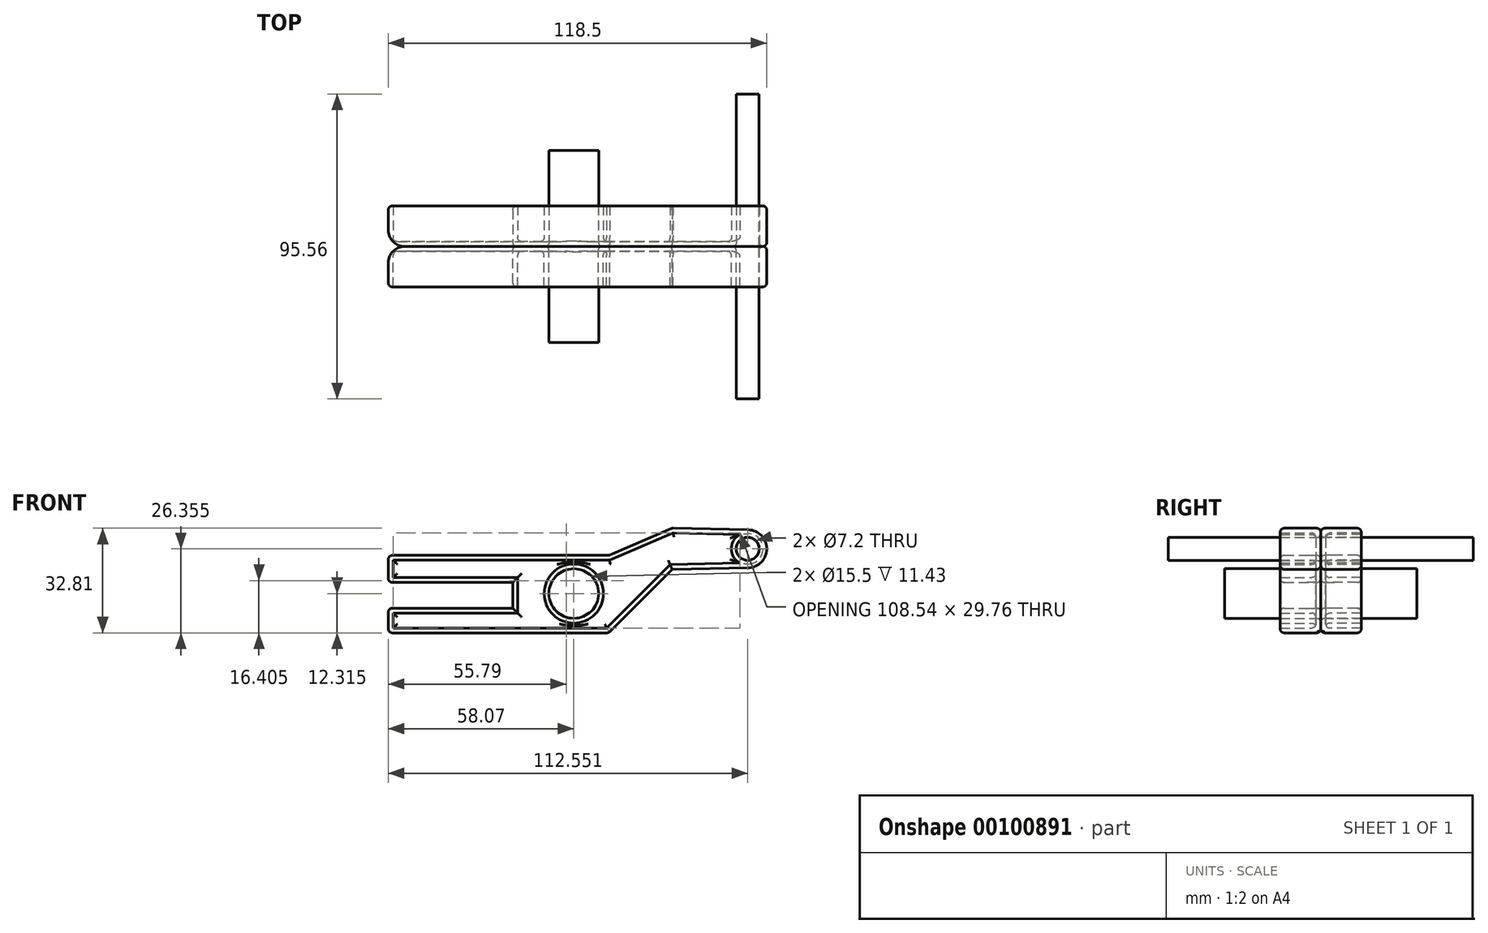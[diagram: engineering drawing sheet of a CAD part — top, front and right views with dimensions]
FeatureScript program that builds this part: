
annotation { "Feature Type Name" : "Feature", "Feature Type Description" : "" }
export const myFeature = defineFeature(function(context is Context, id is Id, definition is map)
    precondition{}
    {
        {
            var Q0;
            Q0=qCreatedBy(makeId("Front.planeOp"),FACE);
            var sketch = newSketch(context, id + "F0", { "sketchPlane" : qUnion([Q0])});
            skLineSegment(sketch, "E0", {"start": v(-58.07, -43.98) * mm, "end": v(10.9, -43.98) * mm});
            skLineSegment(sketch, "E1", {"start": v(10.9, -43.98) * mm, "end": v(30.82, -24.09) * mm});
            skLineSegment(sketch, "E2", {"start": v(30.82, -24.09) * mm, "end": v(54.61, -23.57) * mm});
            skArc(sketch, "E3", {"start": v(54.61, -23.57) * mm, "mid": v(60.43, -17.63) * mm, "end": v(54.61, -11.68) * mm});
            skLineSegment(sketch, "E4", {"start": v(54.61, -11.68) * mm, "end": v(30.82, -11.16) * mm});
            skLineSegment(sketch, "E5", {"start": v(30.82, -11.16) * mm, "end": v(10.9, -19.7) * mm});
            skLineSegment(sketch, "E6", {"start": v(10.9, -19.7) * mm, "end": v(-58.07, -19.7) * mm});
            skLineSegment(sketch, "E7", {"start": v(-58.07, -19.7) * mm, "end": v(-58.07, -28.18) * mm});
            skLineSegment(sketch, "E8", {"start": v(-58.07, -28.18) * mm, "end": v(-19.1, -28.18) * mm});
            skLineSegment(sketch, "E9", {"start": v(-19.1, -28.18) * mm, "end": v(-19.1, -36.23) * mm});
            skLineSegment(sketch, "E10", {"start": v(-19.1, -36.23) * mm, "end": v(-58.07, -36.23) * mm});
            skLineSegment(sketch, "E11", {"start": v(-58.07, -36.23) * mm, "end": v(-58.07, -43.98) * mm});
            skCircle(sketch, "E12", {"center": v(54.48, -17.63) * mm, "radius": 3.6 * mm});
            skCircle(sketch, "E13", {"center": v(0, -31.67) * mm, "radius": 7.75 * mm});
            skSolve(sketch);
        }
        {
            var Q0;
            Q0=makeQuery(id+"F0.imprint","IMPRINT",FACE,{"disambiguationData":[TD([[makeQuery(id+"F0.imprint","IMPRINT",EDGE,{"derivedFrom":sQuery(id+"F0.wireOp",EDGE,"E0")}),1.0]])]});
            extrude(context, id + "F1", {"entities" : qUnion([Q0]), "depth" : 12.7 * mm});
        }
        {
            var Q0;
            Q0=makeQuery(id+"F1.opExtrude","CAP_FACE",FACE,{"disambiguationData":[OSD([sQuery(id+"F0.wireOp",EDGE,"E0"),sQuery(id+"F0.wireOp",EDGE,"E1"),sQuery(id+"F0.wireOp",EDGE,"E2"),sQuery(id+"F0.wireOp",EDGE,"E3"),sQuery(id+"F0.wireOp",EDGE,"E4"),sQuery(id+"F0.wireOp",EDGE,"E5"),sQuery(id+"F0.wireOp",EDGE,"E6"),sQuery(id+"F0.wireOp",EDGE,"E7"),sQuery(id+"F0.wireOp",EDGE,"E8"),sQuery(id+"F0.wireOp",EDGE,"E9"),sQuery(id+"F0.wireOp",EDGE,"E10"),sQuery(id+"F0.wireOp",EDGE,"E11"),sQuery(id+"F0.wireOp",EDGE,"E12"),sQuery(id+"F0.wireOp",EDGE,"E13")])],"isStart":false});
            shell(context, id + "F2", {"entities" : qUnion([Q0]), "thickness" : 1.52 * mm});
        }
        {
            var Q0;
            {var subQ0=sQuery(id+"F0.wireOp",EDGE,"E13");var subQ1=sQuery(id+"F0.wireOp",EDGE,"E12");var subQ2=sQuery(id+"F0.wireOp",EDGE,"E11");var subQ3=sQuery(id+"F0.wireOp",EDGE,"E10");var subQ4=sQuery(id+"F0.wireOp",EDGE,"E9");var subQ5=sQuery(id+"F0.wireOp",EDGE,"E8");var subQ6=sQuery(id+"F0.wireOp",EDGE,"E7");var subQ7=sQuery(id+"F0.wireOp",EDGE,"E6");var subQ8=sQuery(id+"F0.wireOp",EDGE,"E5");var subQ9=sQuery(id+"F0.wireOp",EDGE,"E4");var subQ10=sQuery(id+"F0.wireOp",EDGE,"E3");var subQ11=sQuery(id+"F0.wireOp",EDGE,"E2");var subQ12=sQuery(id+"F0.wireOp",EDGE,"E1");var subQ13=sQuery(id+"F0.wireOp",EDGE,"E0");Q0=makeQuery(id+"F2.opShell","OFFSET_FACE",FACE,{"disambiguationData":[OSD([subQ13,subQ12,subQ11,subQ10,subQ9,subQ8,subQ7,subQ6,subQ5,subQ4,subQ3,subQ2,subQ1,subQ0]),TDD([makeQuery(id+"F1.opExtrude","CAP_FACE",FACE,{"disambiguationData":[OSD([subQ13,subQ12,subQ11,subQ10,subQ9,subQ8,subQ7,subQ6,subQ5,subQ4,subQ3,subQ2,subQ1,subQ0])],"isStart":true})])]});}
            fillet(context, id + "F10", {"entities" : qUnion([Q0]), "radius" : 1.27 * mm, "tangentPropagation" : true, "allowEdgeOverflow" : false});
        }
        {
            var Q0;
            Q0=makeQuery(id+"F1.opExtrude","CAP_EDGE",EDGE,{"disambiguationData":[OSD([sQuery(id+"F0.wireOp",EDGE,"E11")])],"isStart":true});
            var Q1;
            Q1=makeQuery(id+"F1.opExtrude","CAP_EDGE",EDGE,{"disambiguationData":[OSD([sQuery(id+"F0.wireOp",EDGE,"E7")])],"isStart":true});
            fillet(context, id + "F3", {"entities" : qUnion([Q0, Q1]), "radius" : 5.08 * mm, "tangentPropagation" : true, "allowEdgeOverflow" : false});
        }
        {
            var Q0;
            Q0=makeQuery(id+"F1.opExtrude","CAP_EDGE",EDGE,{"disambiguationData":[OSD([sQuery(id+"F0.wireOp",EDGE,"E3")])],"isStart":true});
            var Q1;
            Q1=makeQuery(id+"F1.opExtrude","SWEPT_FACE",FACE,{"disambiguationData":[OSD([sQuery(id+"F0.wireOp",EDGE,"E5")])]});
            var Q2;
            Q2=makeQuery(id+"F1.opExtrude","SWEPT_FACE",FACE,{"disambiguationData":[OSD([sQuery(id+"F0.wireOp",EDGE,"E4")])]});
            var Q3;
            Q3=makeQuery(id+"F1.opExtrude","CAP_FACE",FACE,{"disambiguationData":[OSD([sQuery(id+"F0.wireOp",EDGE,"E0"),sQuery(id+"F0.wireOp",EDGE,"E1"),sQuery(id+"F0.wireOp",EDGE,"E2"),sQuery(id+"F0.wireOp",EDGE,"E3"),sQuery(id+"F0.wireOp",EDGE,"E4"),sQuery(id+"F0.wireOp",EDGE,"E5"),sQuery(id+"F0.wireOp",EDGE,"E6"),sQuery(id+"F0.wireOp",EDGE,"E7"),sQuery(id+"F0.wireOp",EDGE,"E8"),sQuery(id+"F0.wireOp",EDGE,"E9"),sQuery(id+"F0.wireOp",EDGE,"E10"),sQuery(id+"F0.wireOp",EDGE,"E11"),sQuery(id+"F0.wireOp",EDGE,"E12"),sQuery(id+"F0.wireOp",EDGE,"E13")])],"isStart":true});
            fillet(context, id + "F11", {"entities" : qUnion([Q0, Q1, Q2, Q3]), "radius" : 1.27 * mm, "tangentPropagation" : true, "allowEdgeOverflow" : false});
        }
        {
            var Q0;
            Q0=makeQuery(id+"F1.opExtrude","CAP_EDGE",EDGE,{"disambiguationData":[OSD([sQuery(id+"F0.wireOp",EDGE,"E1")])],"isStart":false});
            var Q1;
            Q1=makeQuery(id+"F1.opExtrude","SWEPT_FACE",FACE,{"disambiguationData":[OSD([sQuery(id+"F0.wireOp",EDGE,"E0")])]});
            fillet(context, id + "F4", {"entities" : qUnion([Q0, Q1]), "radius" : 1.27 * mm, "tangentPropagation" : true, "allowEdgeOverflow" : false});
        }
        {
            var Q0;
            Q0=makeQuery(id+"F1.opExtrude","CAP_EDGE",EDGE,{"disambiguationData":[OSD([sQuery(id+"F0.wireOp",EDGE,"E9")])],"isStart":false});
            var Q1;
            Q1=makeQuery(id+"F1.opExtrude","CAP_EDGE",EDGE,{"disambiguationData":[OSD([sQuery(id+"F0.wireOp",EDGE,"E8")])],"isStart":false});
            fillet(context, id + "F5", {"entities" : qUnion([Q0, Q1]), "radius" : 1.27 * mm, "tangentPropagation" : true, "allowEdgeOverflow" : false});
        }
        {
            var Q0;
            Q0=makeQuery(id+"F1.opExtrude","SWEPT_BODY",BODY,{"disambiguationData":[OSD([sQuery(id+"F0.wireOp",EDGE,"E0"),sQuery(id+"F0.wireOp",EDGE,"E1"),sQuery(id+"F0.wireOp",EDGE,"E2"),sQuery(id+"F0.wireOp",EDGE,"E3"),sQuery(id+"F0.wireOp",EDGE,"E4"),sQuery(id+"F0.wireOp",EDGE,"E5"),sQuery(id+"F0.wireOp",EDGE,"E6"),sQuery(id+"F0.wireOp",EDGE,"E7"),sQuery(id+"F0.wireOp",EDGE,"E8"),sQuery(id+"F0.wireOp",EDGE,"E9"),sQuery(id+"F0.wireOp",EDGE,"E10"),sQuery(id+"F0.wireOp",EDGE,"E11"),sQuery(id+"F0.wireOp",EDGE,"E12"),sQuery(id+"F0.wireOp",EDGE,"E13")])]});
            var Q1;
            Q1=qCreatedBy(makeId("Front.planeOp"),FACE);
            mirror(context, id + "F6", {"entities" : qUnion([Q0]), "mirrorPlane" : qUnion([Q1])});
        }
        {
            var Q0;
            Q0=qCreatedBy(makeId("Front.planeOp"),FACE);
            var sketch = newSketch(context, id + "F7", { "sketchPlane" : qUnion([Q0])});
            skCircle(sketch, "E14", {"center": v(0, -31.65) * mm, "radius": 7.77 * mm});
            skPoint(sketch, "E14.first.point", {"position": v(0, -23.88) * mm});
            skPoint(sketch, "E14.second.point", {"position": v(0, -39.42) * mm});
            skPoint(sketch, "E14.third.point", {"position": v(7.75, -31.08) * mm});
            skCircle(sketch, "E15", {"center": v(54.46, -17.66) * mm, "radius": 3.6 * mm});
            skPoint(sketch, "E15.first.point", {"position": v(51.29, -19.34) * mm});
            skPoint(sketch, "E15.second.point", {"position": v(54.15, -14.08) * mm});
            skPoint(sketch, "E15.third.point", {"position": v(57.3, -19.86) * mm});
            skSolve(sketch);
        }
        {
            var Q0;
            Q0=makeQuery(id+"F7.imprint","IMPRINT",FACE,{"disambiguationData":[TD([[makeQuery(id+"F7.imprint","IMPRINT",EDGE,{"derivedFrom":sQuery(id+"F7.wireOp",EDGE,"E14")}),1.0]])]});
            extrude(context, id + "F8", {"entities" : qUnion([Q0]), "endBound" : BoundingType.SYMMETRIC, "depth" : 60.16 * mm});
        }
        {
            var Q0;
            Q0=makeQuery(id+"F7.imprint","IMPRINT",FACE,{"disambiguationData":[TD([[makeQuery(id+"F7.imprint","IMPRINT",EDGE,{"derivedFrom":sQuery(id+"F7.wireOp",EDGE,"E15")}),1.0]])]});
            extrude(context, id + "F9", {"entities" : qUnion([Q0]), "endBound" : BoundingType.SYMMETRIC, "depth" : 95.56 * mm});
        }
    });
